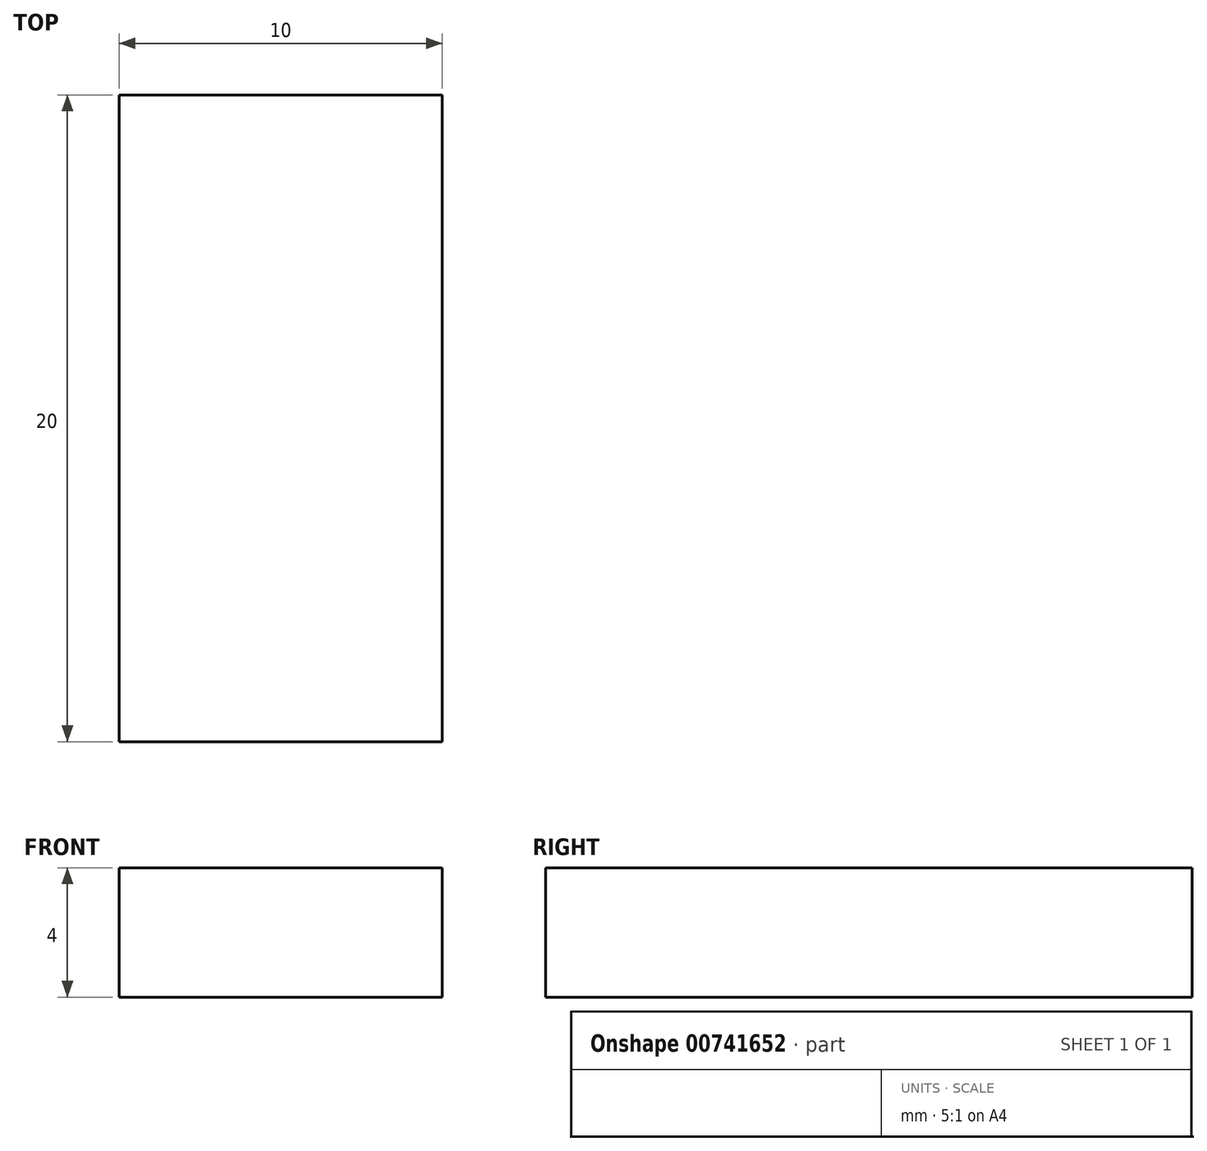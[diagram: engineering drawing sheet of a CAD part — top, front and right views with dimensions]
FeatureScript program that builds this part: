
annotation { "Feature Type Name" : "Feature", "Feature Type Description" : "" }
export const myFeature = defineFeature(function(context is Context, id is Id, definition is map)
    precondition{}
    {
        {
            var Q0;
            Q0=qCreatedBy(makeId("Top.planeOp"),FACE);
            var sketch = newSketch(context, id + "F0", { "sketchPlane" : qUnion([Q0])});
            skLineSegment(sketch, "E0", {"start": v(0, 0) * mm, "end": v(-10, 0) * mm});
            skLineSegment(sketch, "E1", {"start": v(-10, 0) * mm, "end": v(-10, 20) * mm});
            skLineSegment(sketch, "E2", {"start": v(-10, 20) * mm, "end": v(0, 20) * mm});
            skLineSegment(sketch, "E3", {"start": v(0, 20) * mm, "end": v(0, 0) * mm});
            skSolve(sketch);
        }
        {
            var Q0;
            Q0 = qSketchRegion(id + "F0", true);
            extrude(context, id + "F1", {"entities" : qUnion([Q0]), "depth" : 4 * mm, "offsetDistance" : 25 * mm});
        }
    });
